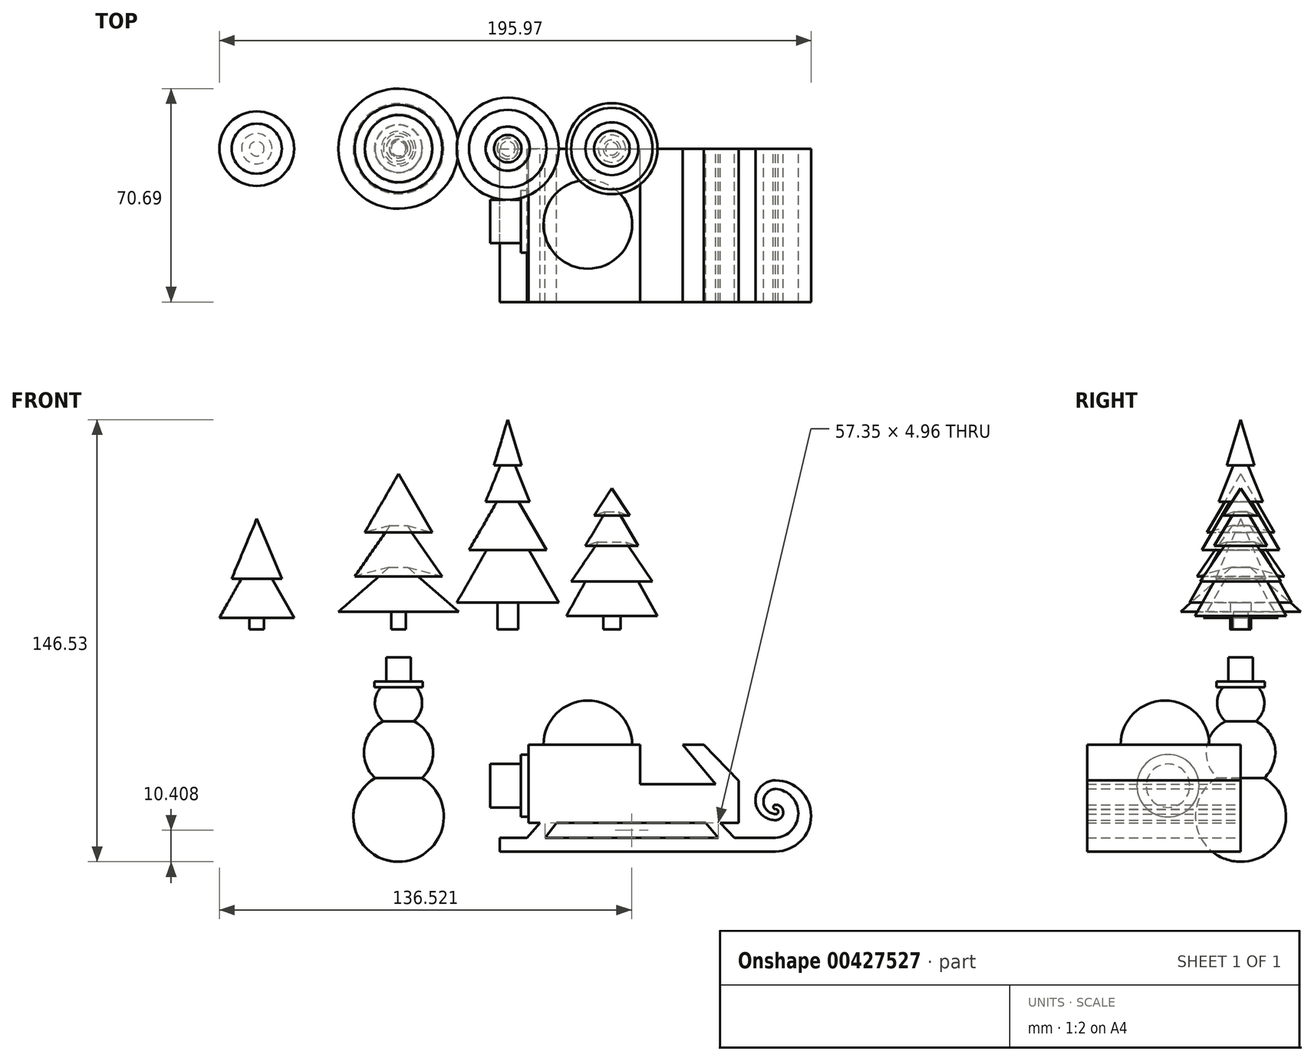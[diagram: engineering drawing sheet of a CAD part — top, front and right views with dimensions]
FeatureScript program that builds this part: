
annotation { "Feature Type Name" : "Feature", "Feature Type Description" : "" }
export const myFeature = defineFeature(function(context is Context, id is Id, definition is map)
    precondition{}
    {
        {
            var Q0;
            Q0=qCreatedBy(makeId("Front.planeOp"),FACE);
            var sketch = newSketch(context, id + "F0", { "sketchPlane" : qUnion([Q0])});
            skLineSegment(sketch, "E0", {"start": v(0, 0) * mm, "end": v(0, 51.53) * mm});
            skLineSegment(sketch, "E1", {"start": v(0, 51.53) * mm, "end": v(-11.15, 32.2) * mm});
            skLineSegment(sketch, "E2", {"start": v(-11.15, 32.2) * mm, "end": v(-2.87, 34.39) * mm});
            skLineSegment(sketch, "E3", {"start": v(-2.87, 34.39) * mm, "end": v(-14.48, 17.6) * mm});
            skLineSegment(sketch, "E4", {"start": v(-14.48, 17.6) * mm, "end": v(-3.1, 20.58) * mm});
            skLineSegment(sketch, "E5", {"start": v(-3.1, 20.58) * mm, "end": v(-19.9, 5.86) * mm});
            skLineSegment(sketch, "E6", {"start": v(-19.9, 5.86) * mm, "end": v(-2.4, 5.86) * mm});
            skLineSegment(sketch, "E7", {"start": v(-2.4, 5.86) * mm, "end": v(-2.4, 0) * mm});
            skLineSegment(sketch, "E8", {"start": v(-2.4, 0) * mm, "end": v(0, 0) * mm});
            skLineSegment(sketch, "E9", {"start": v(70.66, 0) * mm, "end": v(70.66, 46.76) * mm});
            skLineSegment(sketch, "E10", {"start": v(70.66, 46.76) * mm, "end": v(64.77, 37.72) * mm});
            skLineSegment(sketch, "E11", {"start": v(64.77, 37.72) * mm, "end": v(68.57, 38.99) * mm});
            skLineSegment(sketch, "E12", {"start": v(68.57, 38.99) * mm, "end": v(61.9, 27.72) * mm});
            skLineSegment(sketch, "E13", {"start": v(61.9, 27.72) * mm, "end": v(66.15, 28.98) * mm});
            skLineSegment(sketch, "E14", {"start": v(66.15, 28.98) * mm, "end": v(57.18, 15.87) * mm});
            skLineSegment(sketch, "E15", {"start": v(57.18, 15.87) * mm, "end": v(61.9, 15.87) * mm});
            skLineSegment(sketch, "E16", {"start": v(61.9, 15.87) * mm, "end": v(55.57, 4.48) * mm});
            skLineSegment(sketch, "E17", {"start": v(55.57, 4.48) * mm, "end": v(67.76, 4.48) * mm});
            skLineSegment(sketch, "E18", {"start": v(67.76, 4.48) * mm, "end": v(67.76, 0) * mm});
            skLineSegment(sketch, "E19", {"start": v(67.76, 0) * mm, "end": v(70.66, 0) * mm});
            skLineSegment(sketch, "E20", {"start": v(-46.96, 0) * mm, "end": v(-46.96, 36.67) * mm});
            skLineSegment(sketch, "E21", {"start": v(-46.96, 36.67) * mm, "end": v(-55.25, 16.82) * mm});
            skLineSegment(sketch, "E22", {"start": v(-55.25, 16.82) * mm, "end": v(-52, 16.82) * mm});
            skLineSegment(sketch, "E23", {"start": v(-52, 16.82) * mm, "end": v(-59.32, 3.8) * mm});
            skLineSegment(sketch, "E24", {"start": v(-59.32, 3.8) * mm, "end": v(-49.4, 3.8) * mm});
            skLineSegment(sketch, "E25", {"start": v(-49.4, 3.8) * mm, "end": v(-49.4, 0) * mm});
            skLineSegment(sketch, "E26", {"start": v(-49.4, 0) * mm, "end": v(-46.96, 0) * mm});
            skLineSegment(sketch, "E27", {"start": v(36.17, 0) * mm, "end": v(36.17, 69.53) * mm});
            skLineSegment(sketch, "E28", {"start": v(36.17, 69.53) * mm, "end": v(31.62, 54.4) * mm});
            skLineSegment(sketch, "E29", {"start": v(31.62, 54.4) * mm, "end": v(33.73, 54.4) * mm});
            skLineSegment(sketch, "E30", {"start": v(33.73, 54.4) * mm, "end": v(28.85, 42.37) * mm});
            skLineSegment(sketch, "E31", {"start": v(28.85, 42.37) * mm, "end": v(32.6, 42.37) * mm});
            skLineSegment(sketch, "E32", {"start": v(32.6, 42.37) * mm, "end": v(23.32, 26.26) * mm});
            skLineSegment(sketch, "E33", {"start": v(23.32, 26.26) * mm, "end": v(29.18, 26.26) * mm});
            skLineSegment(sketch, "E34", {"start": v(29.18, 26.26) * mm, "end": v(19.25, 8.85) * mm});
            skLineSegment(sketch, "E35", {"start": v(19.25, 8.85) * mm, "end": v(32.76, 8.85) * mm});
            skLineSegment(sketch, "E36", {"start": v(32.76, 8.85) * mm, "end": v(32.76, 0) * mm});
            skLineSegment(sketch, "E37", {"start": v(32.76, 0) * mm, "end": v(36.17, 0) * mm});
            skArc(sketch, "E38", {"start": v(-7.8, -49.2) * mm, "mid": v(-14.43, -66.05) * mm, "end": v(0, -77) * mm});
            skArc(sketch, "E39", {"start": v(-4.99, -30.44) * mm, "mid": v(-11.35, -39.08) * mm, "end": v(-7.8, -49.2) * mm});
            skLineSegment(sketch, "E40.bottom", {"start": v(-7.97, -17.24) * mm, "end": v(-4.06, -17.24) * mm});
            skLineSegment(sketch, "E40.top", {"start": v(-7.97, -19.11) * mm, "end": v(-5.75, -19.11) * mm});
            skLineSegment(sketch, "E40.left", {"start": v(-7.97, -17.24) * mm, "end": v(-7.97, -19.11) * mm});
            skLineSegment(sketch, "E41.top", {"start": v(-4.06, -9.3) * mm, "end": v(0, -9.3) * mm});
            skLineSegment(sketch, "E41.left", {"start": v(-4.06, -17.24) * mm, "end": v(-4.06, -9.3) * mm});
            skLineSegment(sketch, "E42", {"start": v(0, -9.3) * mm, "end": v(0, -77) * mm});
            skArc(sketch, "E43.trimOffspring", {"start": v(-5.75, -19.11) * mm, "mid": v(-7.8, -24.94) * mm, "end": v(-4.99, -30.44) * mm});
            skLineSegment(sketch, "E44.bottom", {"start": v(43.04, -38.25) * mm, "end": v(80.04, -38.25) * mm});
            skLineSegment(sketch, "E44.top", {"start": v(43.04, -64.11) * mm, "end": v(112.61, -64.11) * mm});
            skLineSegment(sketch, "E44.left", {"start": v(43.04, -38.25) * mm, "end": v(43.04, -64.11) * mm});
            skLineSegment(sketch, "E44.right", {"start": v(112.61, -50.2) * mm, "end": v(112.61, -64.11) * mm});
            skLineSegment(sketch, "E45.bottom", {"start": v(33.54, -69.07) * mm, "end": v(124.86, -69.07) * mm});
            skLineSegment(sketch, "E45.top", {"start": v(33.54, -73.61) * mm, "end": v(124.86, -73.61) * mm});
            skLineSegment(sketch, "E45.left", {"start": v(33.54, -69.07) * mm, "end": v(33.54, -73.61) * mm});
            skArc(sketch, "E46", {"start": v(124.86, -73.61) * mm, "mid": v(136.65, -61.82) * mm, "end": v(124.86, -50.04) * mm});
            skArc(sketch, "E47", {"start": v(124.86, -63.2) * mm, "mid": v(127.4, -60.65) * mm, "end": v(124.86, -58.1) * mm});
            skArc(sketch, "E48", {"start": v(124.86, -50.04) * mm, "mid": v(118.21, -56.62) * mm, "end": v(124.86, -63.2) * mm});
            skArc(sketch, "E49", {"start": v(124.86, -69.07) * mm, "mid": v(132.4, -60.98) * mm, "end": v(124.86, -52.88) * mm});
            skArc(sketch, "E50", {"start": v(124.86, -52.88) * mm, "mid": v(120.86, -57.05) * mm, "end": v(124.86, -61.22) * mm});
            skArc(sketch, "E51", {"start": v(124.86, -61.22) * mm, "mid": v(125.79, -60.42) * mm, "end": v(124.86, -59.62) * mm});
            skArc(sketch, "E52", {"start": v(124.86, -58.1) * mm, "mid": v(124.15, -58.86) * mm, "end": v(124.86, -59.62) * mm});
            skLineSegment(sketch, "E53", {"start": v(46.93, -64.11) * mm, "end": v(42.58, -69.07) * mm});
            skLineSegment(sketch, "E54", {"start": v(52.34, -64.11) * mm, "end": v(48.53, -69.07) * mm});
            skLineSegment(sketch, "E55", {"start": v(106.59, -64.11) * mm, "end": v(111.3, -69.07) * mm});
            skLineSegment(sketch, "E56", {"start": v(101.8, -64.11) * mm, "end": v(105.88, -69.07) * mm});
            skLineSegment(sketch, "E57", {"start": v(101.08, -38.25) * mm, "end": v(112.61, -50.2) * mm});
            skLineSegment(sketch, "E58", {"start": v(80.04, -38.25) * mm, "end": v(80.04, -51.32) * mm});
            skLineSegment(sketch, "E59", {"start": v(80.04, -51.32) * mm, "end": v(105.08, -51.32) * mm});
            skLineSegment(sketch, "E60", {"start": v(105.08, -51.32) * mm, "end": v(94.07, -38.25) * mm});
            skLineSegment(sketch, "E61", {"start": v(94.07, -38.25) * mm, "end": v(101.08, -38.25) * mm});
            skSolve(sketch);
        }
        {
            var Q0;
            Q0=makeQuery(id+"F0.imprint","IMPRINT",FACE,{"disambiguationData":[TD([[makeQuery(id+"F0.imprint","IMPRINT",EDGE,{"derivedFrom":sQuery(id+"F0.wireOp",EDGE,"E0")}),1.0]])]});
            var Q1;
            Q1=sQuery(id+"F0.wireOp",EDGE,"E0");
            revolve(context, id + "F1", {"entities" : qUnion([Q0]), "axis" : qUnion([Q1]), "revolveType" : RevolveType.FULL});
        }
        {
            var Q0;
            Q0=makeQuery(id+"F0.imprint","IMPRINT",FACE,{"disambiguationData":[TD([[makeQuery(id+"F0.imprint","IMPRINT",EDGE,{"derivedFrom":sQuery(id+"F0.wireOp",EDGE,"E20")}),1.0]])]});
            var Q1;
            Q1=sQuery(id+"F0.wireOp",EDGE,"E20");
            revolve(context, id + "F2", {"entities" : qUnion([Q0]), "axis" : qUnion([Q1]), "revolveType" : RevolveType.FULL});
        }
        {
            var Q0;
            Q0=makeQuery(id+"F0.imprint","IMPRINT",FACE,{"disambiguationData":[TD([[makeQuery(id+"F0.imprint","IMPRINT",EDGE,{"derivedFrom":sQuery(id+"F0.wireOp",EDGE,"E27")}),1.0]])]});
            var Q1;
            Q1=sQuery(id+"F0.wireOp",EDGE,"E27");
            revolve(context, id + "F3", {"entities" : qUnion([Q0]), "axis" : qUnion([Q1]), "revolveType" : RevolveType.FULL});
        }
        {
            var Q0;
            Q0=makeQuery(id+"F0.imprint","IMPRINT",FACE,{"disambiguationData":[TD([[makeQuery(id+"F0.imprint","IMPRINT",EDGE,{"derivedFrom":sQuery(id+"F0.wireOp",EDGE,"E9")}),1.0]])]});
            var Q1;
            Q1=sQuery(id+"F0.wireOp",EDGE,"E9");
            revolve(context, id + "F4", {"entities" : qUnion([Q0]), "axis" : qUnion([Q1]), "revolveType" : RevolveType.FULL});
        }
        {
            var Q0;
            Q0=makeQuery(id+"F0.imprint","IMPRINT",FACE,{"disambiguationData":[TD([[makeQuery(id+"F0.imprint","IMPRINT",EDGE,{"derivedFrom":sQuery(id+"F0.wireOp",EDGE,"E38")}),1.0]])]});
            var Q1;
            Q1=sQuery(id+"F0.wireOp",EDGE,"E42");
            revolve(context, id + "F5", {"entities" : qUnion([Q0]), "axis" : qUnion([Q1]), "revolveType" : RevolveType.FULL});
        }
        {
            var Q0;
            Q0=makeQuery(id+"F0.imprint","IMPRINT",FACE,{"disambiguationData":[TD([[makeQuery(id+"F0.imprint","IMPRINT",EDGE,{"derivedFrom":sQuery(id+"F0.wireOp",EDGE,"E44.bottom")}),-1.0]])]});
            var Q1;
            {var subQ0=sQuery(id+"F0.wireOp",EDGE,"E53");Q1=makeQuery(id+"F0.imprint","IMPRINT",FACE,{"disambiguationData":[TD([[makeQuery(id+"F0.imprint","IMPRINT",EDGE,{"derivedFrom":subQ0}),1.0]])]});}
            var Q2;
            {var subQ0=sQuery(id+"F0.wireOp",EDGE,"E55");Q2=makeQuery(id+"F0.imprint","IMPRINT",FACE,{"disambiguationData":[TD([[makeQuery(id+"F0.imprint","IMPRINT",EDGE,{"derivedFrom":subQ0}),-1.0]])]});}
            var Q3;
            Q3=makeQuery(id+"F0.imprint","IMPRINT",FACE,{"disambiguationData":[TD([[makeQuery(id+"F0.imprint","IMPRINT",EDGE,{"derivedFrom":sQuery(id+"F0.wireOp",EDGE,"E45.top")}),1.0]])]});
            extrude(context, id + "F6", {"entities" : qUnion([Q0, Q1, Q2, Q3]), "depth" : 50.8 * mm});
        }
        {
            var Q0;
            Q0=makeQuery(id+"F6.opExtrude","SWEPT_FACE",FACE,{"disambiguationData":[OSD([sQuery(id+"F0.wireOp",EDGE,"E44.bottom")])]});
            var sketch = newSketch(context, id + "F7", { "sketchPlane" : qUnion([Q0])});
            skArc(sketch, "E62", {"start": v(62.7, -10.4) * mm, "mid": v(48.02, -25.09) * mm, "end": v(62.7, -39.78) * mm});
            skLineSegment(sketch, "E63", {"start": v(62.7, -39.78) * mm, "end": v(62.7, -10.4) * mm});
            skSolve(sketch);
        }
        {
            var Q0;
            Q0=makeQuery(id+"F7.imprint","IMPRINT",FACE,{"disambiguationData":[TD([[makeQuery(id+"F7.imprint","IMPRINT",EDGE,{"derivedFrom":sQuery(id+"F7.wireOp",EDGE,"E62")}),1.0]])]});
            var Q1;
            Q1=sQuery(id+"F7.wireOp",EDGE,"E63");
            revolve(context, id + "F8", {"operationType" : NewBodyOperationType.ADD, "entities" : qUnion([Q0]), "axis" : qUnion([Q1]), "revolveType" : RevolveType.FULL});
        }
        {
            var Q0;
            Q0=makeQuery(id+"F6.opExtrude","SWEPT_FACE",FACE,{"disambiguationData":[OSD([sQuery(id+"F0.wireOp",EDGE,"E44.left")])]});
            var sketch = newSketch(context, id + "F9", { "sketchPlane" : qUnion([Q0])});
            skCircle(sketch, "E64", {"center": v(24.1, -51.8) * mm, "radius": 10.33 * mm});
            skCircle(sketch, "E65", {"center": v(24.1, -51.8) * mm, "radius": 7.2 * mm});
            skSolve(sketch);
        }
        {
            var Q0;
            Q0=makeQuery(id+"F9.imprint","IMPRINT",FACE,{"disambiguationData":[TD([[makeQuery(id+"F9.imprint","IMPRINT",EDGE,{"derivedFrom":sQuery(id+"F9.wireOp",EDGE,"E65")}),1.0]])]});
            extrude(context, id + "F10", {"entities" : qUnion([Q0]), "operationType" : NewBodyOperationType.ADD, "depth" : 12.7 * mm});
        }
        {
            var Q0;
            Q0=makeQuery(id+"F9.imprint","IMPRINT",FACE,{"disambiguationData":[TD([[makeQuery(id+"F9.imprint","IMPRINT",EDGE,{"derivedFrom":sQuery(id+"F9.wireOp",EDGE,"E64")}),1.0]])]});
            extrude(context, id + "F11", {"entities" : qUnion([Q0]), "operationType" : NewBodyOperationType.ADD, "depth" : 2.54 * mm});
        }
    });
